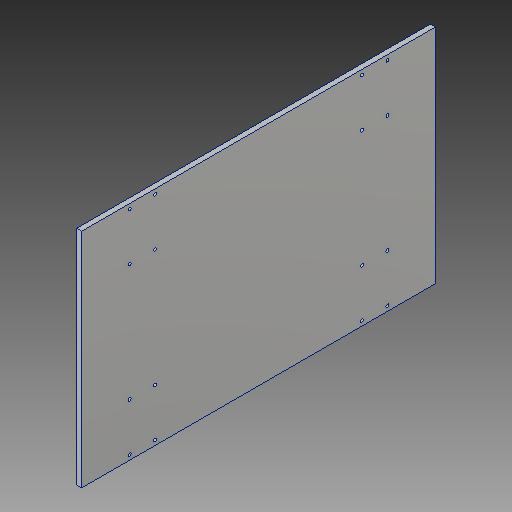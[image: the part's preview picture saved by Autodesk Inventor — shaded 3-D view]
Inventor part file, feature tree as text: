
AUTODESK INVENTOR PART (.ipt)
format: ipt  version: 2017 (Build 210142000, 142)  size: 157,696 bytes
history: native  units: in
note: dims shown in document units (in); Inventor stores cm internally (conversion verified against a paired STEP export)
features: extrude x1, sketch x1
ambient origin geometry x8: Origin, YZ Plane, XZ Plane, XY Plane, X Axis, Y Axis, Z Axis, Center Point
bodies: Solid1 (feature_tree)
feature tree (2):
  extrude  "Extrusion1"  Depth=17.5in
  sketch  "Sketch1"  dims[d0=11.0in d1=17.5in d2=0.153in d3=0.153in d4=1.26in d5=0.236in d6=0.236in d7=2.37in d8=0.153in d9=0.153in d10=2.364in d11=2.364in d12=2.37in d13=0.153in d14=0.153in d15=0.153in d16=0.153in d17=2.37in d18=2.37in d19=0.236in d20=0.236in d22=2.364in d23=2.364in d24=1.26in d25=0.153in d26=0.153in d27=0.236in d28=0.236in d29=0.153in d30=0.153in d32=1.26in d33=1.26in d34=2.37in d35=2.37in d36=0.153in d37=0.153in d38=0.153in d39=0.153in d40=0.25in d41=0.0in]
